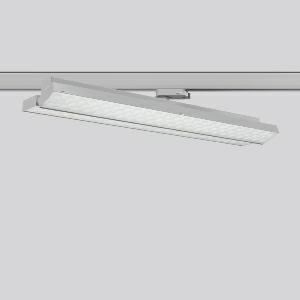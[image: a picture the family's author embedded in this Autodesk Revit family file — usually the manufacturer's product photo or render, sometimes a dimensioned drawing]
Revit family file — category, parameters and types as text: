
# Revit family: tx-move_742163_004_1_3b4e
name_source: partatom
category: Lighting Fixtures
units: mm (PartAtom-declared; Revit-internal decimal feet)

## family parameters
Cut with Voids When Loaded = No
Host = Face
Light Source = No
Part Type = Normal
Room Calculation Point = No
Round Connector Dimension = Use Diameter
Shared = No

## types (1)
- MultiLumen 1 (1 x LED Modul 840, 2950 lm, 4000)
    Apparent Load = 41 VA
    CIE Flux Codes = 65 90 98 100 100
    Color Rendering = 80
    Color Temperature = 4000
    Default Elevation = 1800 mm
    Description = Series: TX-MOVE
Multifunctional surface-mounted spotlight for area lighting. Very flat design. Housing: sheet steel, powder-coated. Rotation range: 356°. Swivel range: 90°. Consistent alignment possible with visible tilt scale. High-efficiency LED units with optimum light control thanks to clear plastic (PC) lens optics. Spezielle Mikrostrukturen reduzieren Gelbsaum. Asymmetrical light distribution. With multi adaptor for 3-circuit tracks 230 V. Suitable for Track on ceiling. MultiLumen: Luminous flux adjustable in 3 steps. Factory setting is the highest luminous flux. Environmentally friendly and resource-saving due to replaceable and recyclable components. 
Colour: silver, matt (approx. RAL 9006)
Length: 570 mm
Width: 119 mm
Height: 92 mm
Lamp: LED
Socket: without socket
Colour temperature: 4000K
Colour rendering index (CRI): 80
System power: 41 W
Rated luminous flux: 5900 lm
Luminous efficiency: 144 lm/W
System power 2: 57 W
Rated luminous flux 2: 8000 lm
Luminous efficiency 2: 140 lm/W
System power 3: 73 W
Rated luminous flux 3: 9750 lm
Luminous efficiency 3: 134 lm/W
Control gear: Regulated power supply
Protection class: I
Type of protection: IP 20
    Height = 75 mm
    Lamp = 1 x LED Modul 840
    Lamp Light Flux = 2950 lm
    Lamp count = 1
    Length = 569 mm
    Lifetime = 50000 h
    Luminous efficacy = 144 lm/W
    Manufacturer = RZB
    ModVariant = No
    Model = 742163.004.1
    Mounting Place = Ceiling
    Mounting Type = Surface mounted
    Number of Poles = 1
    OnlyDefault = Yes
    Power Factor = 1
    Product Name = TX-MOVE
    Product group = Track mounted projectors
    ProductGroupID = 301
    Protection Class = Protection class I
    Protection Degree = IP 20
    RLX_Detail_Level = 1
    RLX_Emergency_Light_Flux = 0 lm
    RLX_Emergency_Type = 0
    RLX_Emergency_Type_DB = No
    RlxData = <blob elided: 53853 chars, md5=48a047a1>
    Socket = socket
    Standby Power = 0 W
    System Light Flux = 5900 lm
    System Power = 41 W
    Type Comments = MultiLumen 1
    Type Image = 742162.004.jpg
    URL = http://relux.com
    VarID = multilumen_1
    Voltage = 0 V
    Weight = 0.00 kg
    Width = 119 mm

## geometry (parser evidence)
native form markers: Blend x4, Sweep x16
no freeform markers — native parametric forms only
